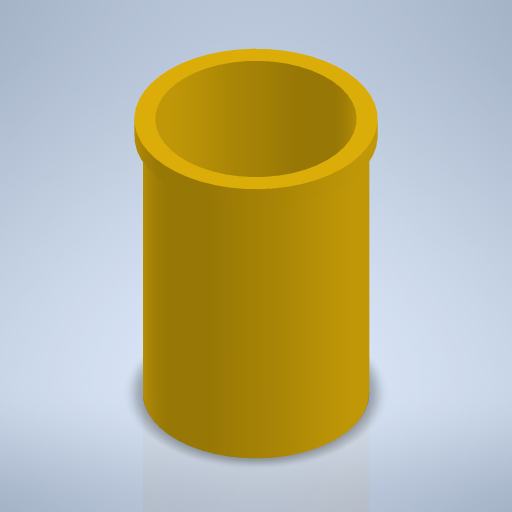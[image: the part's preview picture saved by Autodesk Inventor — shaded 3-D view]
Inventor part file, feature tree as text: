
AUTODESK INVENTOR PART (.ipt)
format: ipt  version: 2024 (Build 280153000, 153)  size: 225,792 bytes
history: native  units: mm
features: sketch x2, revolve x1, hole x1
ambient origin geometry x8: Origin, YZ Plane, XZ Plane, XY Plane, X Axis, Y Axis, Z Axis, Center Point
bodies: Volumenkörper1 (feature_tree)
feature tree (4):
  revolve  "Umdrehung1"
  hole  "Bohrung1"  [1 undecoded]
  sketch  "Skizze1"  dims[d0=40.0mm d1=37.5mm]
  sketch  "Skizze2"  dims[d2=29.0mm d3=27.0mm d4=90.0deg d5=24.0mm d6=6.0mm d7=4.0mm d8=2.0mm d9=90.0deg d10=8.0mm d11=0.0mm]
note: 1 required parameter value undecoded (feature->parameter linkage not recoverable at this tier; creation-order binding heuristic only, values carry confidence <= 0.55)
